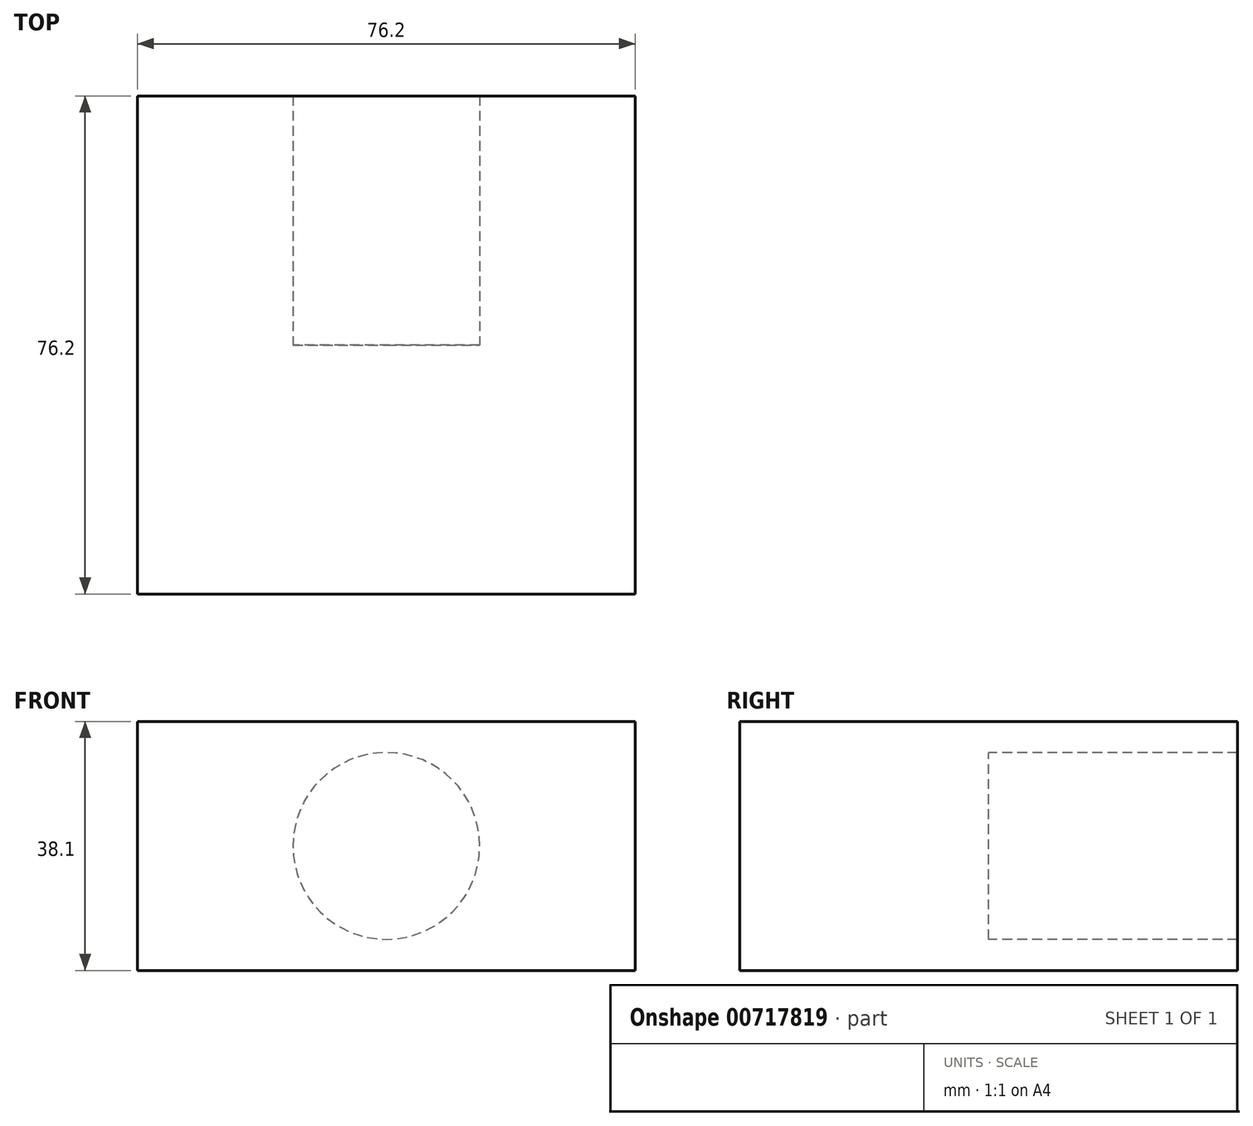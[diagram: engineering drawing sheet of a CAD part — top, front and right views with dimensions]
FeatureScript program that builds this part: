
annotation { "Feature Type Name" : "Feature", "Feature Type Description" : "" }
export const myFeature = defineFeature(function(context is Context, id is Id, definition is map)
    precondition{}
    {
        {
            var Q0;
            Q0=qCreatedBy(makeId("Front.planeOp"),FACE);
            var sketch = newSketch(context, id + "F0", { "sketchPlane" : qUnion([Q0])});
            skLineSegment(sketch, "E0.bottom", {"start": v(38.1, -19.05) * mm, "end": v(-38.1, -19.05) * mm});
            skLineSegment(sketch, "E0.top", {"start": v(38.1, 19.05) * mm, "end": v(-38.1, 19.05) * mm});
            skLineSegment(sketch, "E0.left", {"start": v(38.1, -19.05) * mm, "end": v(38.1, 19.05) * mm});
            skLineSegment(sketch, "E0.right", {"start": v(-38.1, -19.05) * mm, "end": v(-38.1, 19.05) * mm});
            skPoint(sketch, "E0.middle", {"position": v(0, 0) * mm});
            skLineSegment(sketch, "E1.bottom", {"start": v(14.29, 36.8) * mm, "end": v(-14.29, 36.8) * mm});
            skLineSegment(sketch, "E1.top", {"start": v(14.29, -36.8) * mm, "end": v(-14.29, -36.8) * mm});
            skLineSegment(sketch, "E1.left", {"start": v(14.29, 36.8) * mm, "end": v(14.29, -36.8) * mm});
            skLineSegment(sketch, "E1.right", {"start": v(-14.29, 36.8) * mm, "end": v(-14.29, -36.8) * mm});
            skSolve(sketch);
        }
        {
            var Q0;
            {var subQ0=sQuery(id+"F0.wireOp",EDGE,"E0.right");Q0=makeQuery(id+"F0.imprint","IMPRINT",FACE,{"disambiguationData":[TD([[makeQuery(id+"F0.imprint","IMPRINT",EDGE,{"derivedFrom":subQ0}),-1.0]])]});}
            var Q1;
            {var subQ0=sQuery(id+"F0.wireOp",EDGE,"E0.left");Q1=makeQuery(id+"F0.imprint","IMPRINT",FACE,{"disambiguationData":[TD([[makeQuery(id+"F0.imprint","IMPRINT",EDGE,{"derivedFrom":subQ0}),1.0]])]});}
            var Q2;
            {var subQ0=sQuery(id+"F0.wireOp",EDGE,"E1.left");var subQ1=sQuery(id+"F0.wireOp",EDGE,"E0.bottom");var subQ2=makeQuery(id+"F0.imprint","INTERSECT",VERTEX,{"derivedFrom":[subQ1,subQ0]});Q2=makeQuery(id+"F0.imprint","IMPRINT",FACE,{"disambiguationData":[TD([[makeQuery(id+"F0.imprint","IMPRINT",EDGE,{"disambiguationData":[TD([[subQ2,-1.0]])],"derivedFrom":subQ1}),-1.0]])]});}
            extrude(context, id + "F1", {"entities" : qUnion([Q0, Q1, Q2]), "endBound" : BoundingType.SYMMETRIC, "depth" : 76.2 * mm, "offsetDistance" : 25.4 * mm});
        }
        {
            var Q0;
            Q0=sQuery(id+"F0.wireOp",VERTEX,"E0.middle");
            var Q1;
            Q1=makeQuery(id+"F1.opExtrude","SWEPT_BODY",BODY,{"disambiguationData":[OSD([sQuery(id+"F0.wireOp",EDGE,"E0.bottom"),sQuery(id+"F0.wireOp",EDGE,"E0.top"),sQuery(id+"F0.wireOp",EDGE,"E0.left"),sQuery(id+"F0.wireOp",EDGE,"E0.right")])]});
            hole(context, id + "F2", {"style" : HoleStyle.C_BORE, "endStyle" : HoleEndStyle.THROUGH, "holeDiameter" : 28.57 * mm, "cBoreDiameter" : 28.57 * mm, "cBoreDepth" : 6.35 * mm, "majorDiameter" : 6.35 * mm, "isTappedThrough" : true, "tappedDepth" : 12.7 * mm, "tapClearance" : 3, "locations" : qUnion([Q0]), "scope" : qUnion([Q1])});
        }
    });
